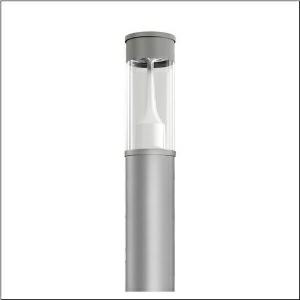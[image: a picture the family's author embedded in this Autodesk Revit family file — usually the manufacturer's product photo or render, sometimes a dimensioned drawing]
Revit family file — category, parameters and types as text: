
# Revit family: city-light_400_iq___st1_2a_5xa5305ef14hp_9457
name_source: partatom
category: Lighting Fixtures
units: mm (PartAtom-declared; Revit-internal decimal feet)

## family parameters
Cut with Voids When Loaded = No
Host = Face
Light Source = No
Part Type = Normal
Room Calculation Point = No
Round Connector Dimension = Use Diameter
Shared = No

## types (1)
- --- (1 x LED, 4730 lm, 33.6 W, 3000K)
    Apparent Load = 34 VA
    CIE Flux Codes = 22 61 94 96 100
    Color Rendering = 70
    Color Temperature = 3000K
    Default Elevation = 1800 mm
    Description = City-Light 400 iQ, light pillar, Module 540 iQ-SR, primary light control with 3 zone facetted reflector, of plastic, silver coated, highly specular, structured, primary optical cover: cover, of PMMA, transparent, partly coated, light distribution: ST1.2a, primary light characteristic: asymmetric, LED, High Power LED, rated luminous flux: 4.730lm, luminous efficacy: 141lm/W, light colour: 730, colour temperature: 3000K, control gear: iQ Street-Remote, control: pre-setting: logarithmic dimming characteristic, Street-Remote, Auto-Match, Temp-Guard, Lumen-Switch, Night-Set, Smart-Wire, Light-Fading, Desk-Remote (wireless, voltage-free reading and setting of iQ features in the workshop via application-optimized NFC function/RFID function), optimised constant luminous flux control (CLO 2.0), with terminal, 6-pole, max. 2.5mm², mains connection: 230..240V, AC, 50/60Hz, start of lifetime: 34W, end of service life: 36W, reduction: 15W, luminaire housing, cylindrical, of extruded aluminium section, coated, Siteco® metallic grey (DB 702S), length: 4.694mm, diameter: 200mm, Module 540 iQ-SR, traffic white (RAL 9016), equipment: Power, protection rating (complete): IP65, insulation class (complete): insulation class II (safety insulation), certification: CE, ENEC, VDE, packaging unit: 1 piece

Light Distribution: ST1.2a
    Height = 500 mm
    Lamp = 1 x LED
    Lamp Light Flux = 4730 lm
    Lamp Power = 33.6 W
    Lamp count = 1
    Length = 200 mm  [stored 0.656168 ft]
    Luminous efficacy = 141 lm/W
    Manufacturer = Siteco
    ModVariant = No
    Model = 5XA5305EF14HP
    Mounting Place = Floor
    Mounting Type = Freestanding
    Number of Poles = 1
    OnlyDefault = Yes
    Power Factor = 1
    Product Name = City-Light 400 iQ | ST1.2a
    Product group = light pillar
    ProductGroupID = 1301
    Protection Class = Protection class II
    Protection Degree = IP 65
    RLX_Detail_Level = 1
    RLX_Emergency_Light_Flux = 0 lm
    RLX_Emergency_Type = 0
    RLX_Emergency_Type_DB = No
    RlxData = <blob elided: 53525 chars, md5=c2c72fe4>
    Socket = socket
    Standby Power = 0 W
    System Light Flux = 4730 lm
    System Power = 34 W
    Type Comments = factory setting: luminous flux: 100 % | dim-lin: 254 | 695 mA
    Type Image = l_1006916.jpg
    URL = http://relux.com
    VarID = @adj_214161
    Voltage = 0 V
    Weight = 0.00 kg
    Width = 0 mm  [stored 0 ft]

note: [stored X ft] marks values corroborated as IEEE doubles in the binary element streams (Revit-internal decimal feet)

## geometry (parser evidence)
native form markers: Blend x4, Sweep x9
no freeform markers — native parametric forms only
